# Revit family: Bathtub-American_Standard-Studio-2946.X02_Series
name_source: partatom
category: Plumbing Fixtures
units: mm (PartAtom-declared; Revit-internal decimal feet)

## family parameters
Always vertical = No
Cut with Voids When Loaded = No
OmniClass Number = 23.45.05.14.21.11
OmniClass Title = Bath/Shower Units
Part Type = Normal
Room Calculation Point = No
Round Connector Dimension = Use Diameter
Shared = Yes
Work Plane-Based = Yes

## types (2) — shared parameters
ADA Compliant = Yes
Assembly Code = D2010510
CSA Compliance = B45.5-11
CWFU = 3
Default Elevation = 0"
Finish = High Gloss Acrylic-American Standard-011-Arctic White
HWFU = 3
Height = 18"
IAPMO Compliance = Z124-2011
Installation Type = Recess Installation
Length = 60"
Manufacturer = American Standard
Material = High Gloss Acrylic-American Standard-011-Arctic White
Price = Prices may vary. Please consult Manufacturer Representative for most up-to-date price list.
Product Documentation Link = https://americanstandard.box.com
Product Page URL = https://www.americanstandard-us.com
Revised Date = 04/29/22
Shipping Weight = 50 lb
URL = https://www.americanstandard-us.com
Vent Connection = No
WFU = 4
Warranty Information = Limited Lifetime Warranty
Waste Connection = Yes
Waste Connection Diameter = 2"
Waste Connection Radius = 1"
Width = 32"
cUPC Compliant = Yes

## per-type parameters (varying)
| type | CW Connection | Connector Location | Description | HW Connection | Tub Geometry |
| 2946.212.011 | No | 9 3/4" | Studio 60" x 32" Bathing Pool with Fold Over Edge and Left Side Drain | No | Bathtub-American_Standard-Studio-2946.212 : 2946.212.011 |
| 2946.112.011 | Yes | 50 1/4" | Studio 60" x 32" Bathing Pool with Fold Over Edge and Right Side Drain | Yes | Bathtub-American_Standard-Studio-2946.112 : 2946.112.011 |

note: column(s) folded — value = type name in every type: Model

## geometry (parser evidence)
native form markers: Sweep x11
no freeform markers — native parametric forms only
